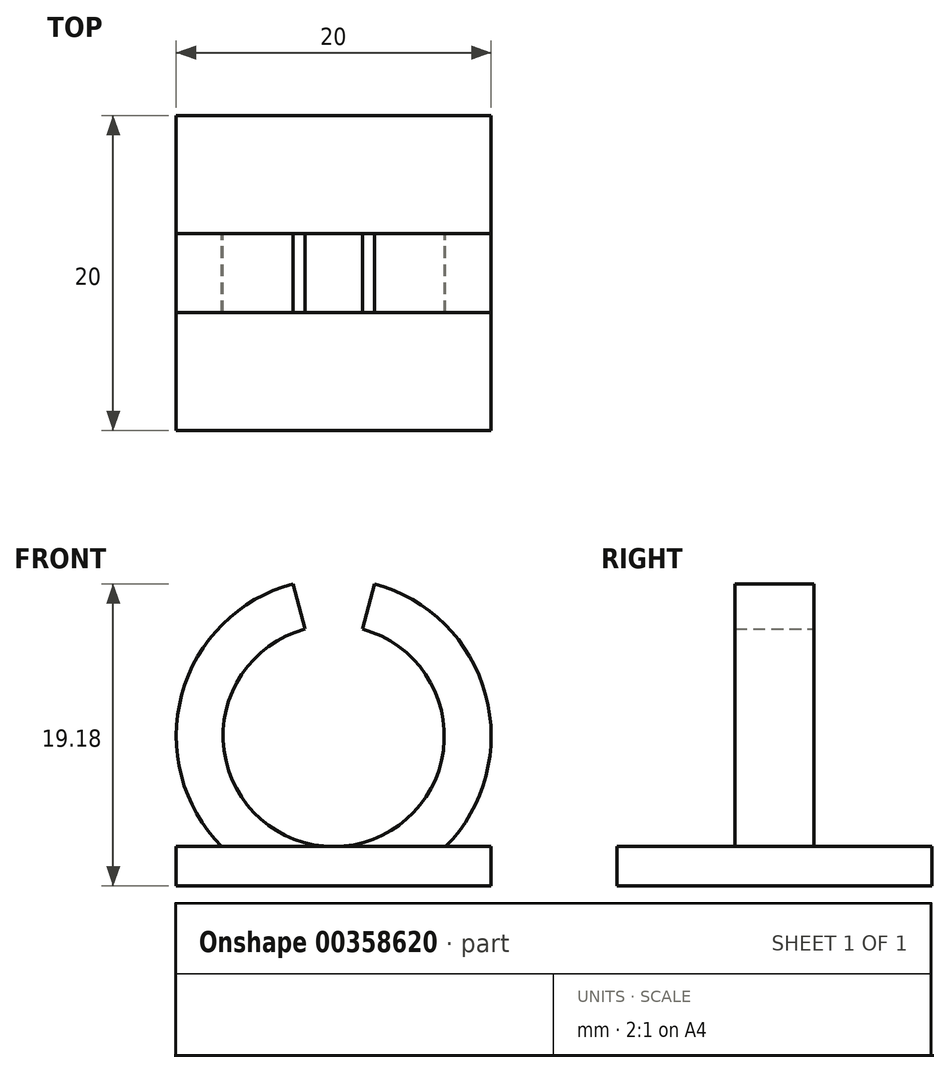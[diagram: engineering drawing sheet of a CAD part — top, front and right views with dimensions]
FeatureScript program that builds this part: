
annotation { "Feature Type Name" : "Feature", "Feature Type Description" : "" }
export const myFeature = defineFeature(function(context is Context, id is Id, definition is map)
    precondition{}
    {
        {
            var Q0;
            Q0=qCreatedBy(makeId("Top.planeOp"),FACE);
            var sketch = newSketch(context, id + "F0", { "sketchPlane" : qUnion([Q0])});
            skLineSegment(sketch, "E0.bottom", {"start": v(-10, 10) * mm, "end": v(10, 10) * mm});
            skLineSegment(sketch, "E0.top", {"start": v(-10, -10) * mm, "end": v(10, -10) * mm});
            skLineSegment(sketch, "E0.left", {"start": v(-10, 10) * mm, "end": v(-10, -10) * mm});
            skLineSegment(sketch, "E0.right", {"start": v(10, 10) * mm, "end": v(10, -10) * mm});
            skSolve(sketch);
        }
        {
            var Q0;
            Q0=makeQuery(id+"F0.imprint","IMPRINT",FACE,{"disambiguationData":[TD([[makeQuery(id+"F0.imprint","IMPRINT",EDGE,{"derivedFrom":sQuery(id+"F0.wireOp",EDGE,"E0.bottom")}),-1.0]])]});
            extrude(context, id + "F1", {"entities" : qUnion([Q0]), "depth" : 2.5 * mm});
        }
        {
            var Q0;
            Q0=qCreatedBy(makeId("Front.planeOp"),FACE);
            var sketch = newSketch(context, id + "F2", { "sketchPlane" : qUnion([Q0])});
            skLineSegment(sketch, "E1", {"start": v(-1.82, 16.31) * mm, "end": v(-1.82, 16.31) * mm});
            skArc(sketch, "E2", {"start": v(-2.59, 19.18) * mm, "mid": v(-10, 9.76) * mm, "end": v(-3.05, 0) * mm});
            skLineSegment(sketch, "E3", {"start": v(0, 9.52) * mm, "end": v(-1.82, 16.31) * mm, "construction": true});
            skArc(sketch, "E4", {"start": v(-1.82, 16.31) * mm, "mid": v(0, 2.5) * mm, "end": v(1.82, 16.31) * mm});
            skLineSegment(sketch, "E5.trimOffspring", {"start": v(1.82, 16.31) * mm, "end": v(0, 9.52) * mm, "construction": true});
            skPoint(sketch, "E6.start.orphan", {"position": v(0, 19.15) * mm});
            skPoint(sketch, "E7", {"position": v(-3.05, 0) * mm});
            skPoint(sketch, "E8", {"position": v(3.05, 0) * mm});
            skArc(sketch, "E9.trimOffspring", {"start": v(3.05, 0) * mm, "mid": v(10, 9.76) * mm, "end": v(2.59, 19.18) * mm});
            skLineSegment(sketch, "E10", {"start": v(-2.59, 19.18) * mm, "end": v(-1.82, 16.31) * mm});
            skLineSegment(sketch, "E11", {"start": v(1.82, 16.31) * mm, "end": v(2.59, 19.18) * mm});
            skLineSegment(sketch, "E12", {"start": v(-3.05, 0) * mm, "end": v(3.05, 0) * mm});
            skSolve(sketch);
        }
        {
            var Q0;
            Q0=makeQuery(id+"F2.imprint","IMPRINT",FACE,{"disambiguationData":[TD([[makeQuery(id+"F2.imprint","IMPRINT",EDGE,{"derivedFrom":sQuery(id+"F2.wireOp",EDGE,"E2")}),1.0]])]});
            extrude(context, id + "F3", {"entities" : qUnion([Q0]), "operationType" : NewBodyOperationType.ADD, "endBound" : BoundingType.SYMMETRIC, "depth" : 3 * mm});
        }
        {
            var Q0;
            Q0 = qSketchRegion(id + "F2", true);
            extrude(context, id + "F4", {"entities" : qUnion([Q0]), "operationType" : NewBodyOperationType.ADD, "endBound" : BoundingType.SYMMETRIC, "depth" : 5 * mm});
        }
        {
            var Q0;
            Q0 = qSketchRegion(id + "F2", true);
            extrude(context, id + "F5", {"entities" : qUnion([Q0]), "operationType" : NewBodyOperationType.ADD, "endBound" : BoundingType.SYMMETRIC, "depth" : 4 * mm});
        }
    });
